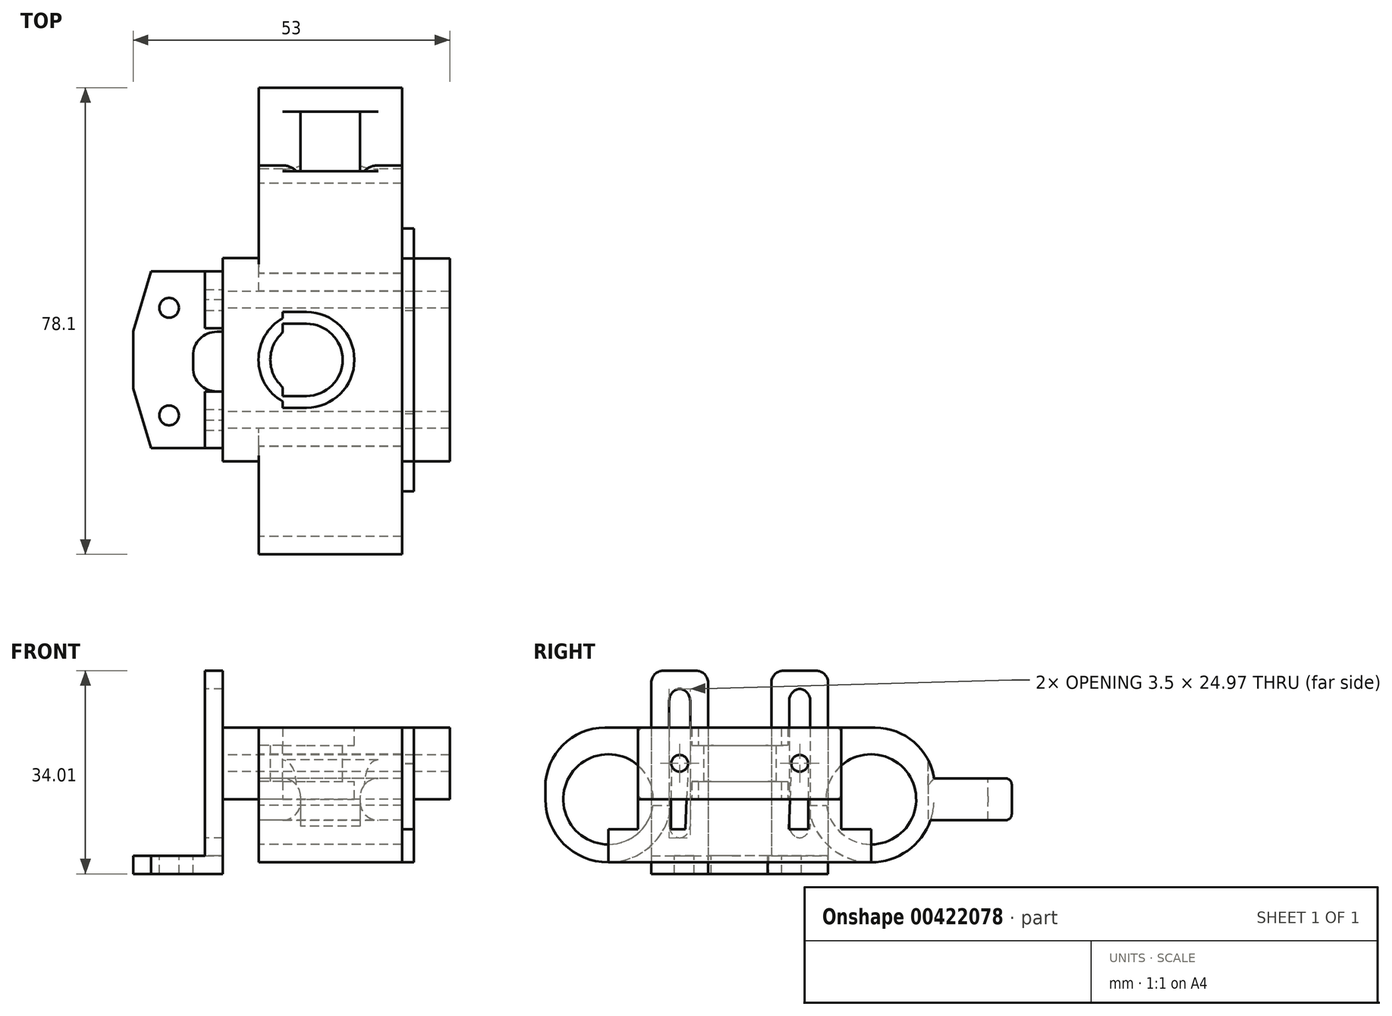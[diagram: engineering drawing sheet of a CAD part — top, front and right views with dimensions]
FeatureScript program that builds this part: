
annotation { "Feature Type Name" : "Feature", "Feature Type Description" : "" }
export const myFeature = defineFeature(function(context is Context, id is Id, definition is map)
    precondition{}
    {
        {
            var Q0;
            Q0=qCreatedBy(makeId("Right.planeOp"),FACE);
            var sketch = newSketch(context, id + "F0", { "sketchPlane" : qUnion([Q0])});
            skCircle(sketch, "E0", {"center": v(0, 0) * mm, "radius": 7.55 * mm});
            skCircle(sketch, "E1", {"center": v(44, 0) * mm, "radius": 7.55 * mm});
            skSolve(sketch);
        }
        {
            var Q0;
            Q0=makeQuery(id+"F0.imprint","IMPRINT",FACE,{"disambiguationData":[TD([[makeQuery(id+"F0.imprint","IMPRINT",EDGE,{"derivedFrom":sQuery(id+"F0.wireOp",EDGE,"E0")}),1.0]])]});
            var Q1;
            Q1=makeQuery(id+"F0.imprint","IMPRINT",FACE,{"disambiguationData":[TD([[makeQuery(id+"F0.imprint","IMPRINT",EDGE,{"derivedFrom":sQuery(id+"F0.wireOp",EDGE,"E1")}),1.0]])]});
            extrude(context, id + "F1", {"entities" : qUnion([Q0, Q1]), "depth" : 24 * mm});
        }
        {
            var Q0;
            Q0=qCreatedBy(makeId("Right.planeOp"),FACE);
            var sketch = newSketch(context, id + "F2", { "sketchPlane" : qUnion([Q0])});
            skCircle(sketch, "E2.0.0", {"center": v(0, 0) * mm, "radius": 7.55 * mm, "construction": true});
            skCircle(sketch, "E3.0.0", {"center": v(44, 0) * mm, "radius": 7.55 * mm, "construction": true});
            skLineSegment(sketch, "E4", {"start": v(7.55, 0) * mm, "end": v(22, 0) * mm, "construction": true});
            skLineSegment(sketch, "E5", {"start": v(22, 0) * mm, "end": v(36.45, 0) * mm, "construction": true});
            skLineSegment(sketch, "E6", {"start": v(22, 0) * mm, "end": v(22, 12.75) * mm});
            skLineSegment(sketch, "E7", {"start": v(22, 12.75) * mm, "end": v(13.97, 12.75) * mm});
            skLineSegment(sketch, "E8", {"start": v(13.97, 12.75) * mm, "end": v(13.97, 9.05) * mm});
            skLineSegment(sketch, "E9", {"start": v(13.97, 9.05) * mm, "end": v(15.95, 9.05) * mm});
            skLineSegment(sketch, "E10", {"start": v(15.95, 9.05) * mm, "end": v(15.95, 3) * mm});
            skLineSegment(sketch, "E11", {"start": v(15.95, 3) * mm, "end": v(13.98, 3) * mm});
            skLineSegment(sketch, "E12", {"start": v(13.97, 3) * mm, "end": v(13.97, 0) * mm});
            skLineSegment(sketch, "E13", {"start": v(13.98, 0) * mm, "end": v(22, 0) * mm});
            skSolve(sketch);
        }
        {
            var Q0;
            Q0=qCreatedBy(makeId("Right.planeOp"),FACE);
            var sketch = newSketch(context, id + "F3", { "sketchPlane" : qUnion([Q0])});
            skLineSegment(sketch, "E14", {"start": v(-10.55, 0) * mm, "end": v(54.55, 0) * mm});
            skLineSegment(sketch, "E15", {"start": v(54.55, 12) * mm, "end": v(-10.55, 12) * mm});
            skLineSegment(sketch, "E16", {"start": v(-10.55, 12) * mm, "end": v(-10.55, 0) * mm});
            skCircle(sketch, "E17.0", {"center": v(0, 0) * mm, "radius": 7.55 * mm, "construction": true});
            skCircle(sketch, "E18.0", {"center": v(44, 0) * mm, "radius": 7.55 * mm, "construction": true});
            skArc(sketch, "E19.0", {"start": v(33.45, 0) * mm, "mid": v(44, -10.55) * mm, "end": v(54.55, 0) * mm});
            skArc(sketch, "E20.0", {"start": v(-10.55, 0) * mm, "mid": v(0, -10.55) * mm, "end": v(10.55, 0) * mm});
            skLineSegment(sketch, "E21", {"start": v(54.55, 0) * mm, "end": v(54.55, 12) * mm});
            skLineSegment(sketch, "E22", {"start": v(54.55, 3.5) * mm, "end": v(67.55, 3.5) * mm});
            skLineSegment(sketch, "E23", {"start": v(67.55, 3.5) * mm, "end": v(67.55, -3.5) * mm});
            skLineSegment(sketch, "E24", {"start": v(67.55, -3.5) * mm, "end": v(53.95, -3.5) * mm});
            skSolve(sketch);
        }
        {
            var Q0;
            Q0 = qSketchRegion(id + "F3", true);
            extrude(context, id + "F4", {"entities" : qUnion([Q0]), "depth" : 24 * mm});
        }
        {
            var Q0;
            Q0 = qSketchRegion(id + "F0", true);
            var Q1;
            Q1 = qConstructionFilter(qBodyType(qCreatedBy(id + "F0" ,EDGE), BodyType.WIRE), ConstructionObject.NO);
            extrude(context, id + "F5", {"entities" : qUnion([Q0]), "operationType" : NewBodyOperationType.REMOVE, "surfaceEntities" : qUnion([Q1]), "endBound" : BoundingType.THROUGH_ALL, "depth" : 25 * mm});
        }
        {
            var Q0;
            Q0=qCreatedBy(makeId("Top.planeOp"),FACE);
            var sketch = newSketch(context, id + "F6", { "sketchPlane" : qUnion([Q0])});
            skLineSegment(sketch, "E25.0", {"start": v(0, 13.98) * mm, "end": v(0, 22) * mm, "construction": true});
            skLineSegment(sketch, "E26", {"start": v(0, 14) * mm, "end": v(8, 14) * mm});
            skLineSegment(sketch, "E27", {"start": v(8, 22) * mm, "end": v(0, 22) * mm, "construction": true});
            skLineSegment(sketch, "E28.MirrorCS", {"start": v(0, 30) * mm, "end": v(8, 30) * mm});
            skArc(sketch, "E29", {"start": v(8, 14) * mm, "mid": v(16, 22) * mm, "end": v(8, 30) * mm});
            skSolve(sketch);
        }
        {
            var Q0;
            Q0=makeQuery(id+"F2.imprint","IMPRINT",FACE,{"disambiguationData":[TD([[makeQuery(id+"F2.imprint","IMPRINT",EDGE,{"derivedFrom":sQuery(id+"F2.wireOp",EDGE,"E6")}),1.0]])]});
            var Q1;
            Q1=sQuery(id+"F6.wireOp",EDGE,"E26");
            var Q2;
            Q2=sQuery(id+"F6.wireOp",EDGE,"E29");
            var Q3;
            Q3=sQuery(id+"F6.wireOp",EDGE,"E28.MirrorCS");
            sweep(context, id + "F7", {"operationType" : NewBodyOperationType.REMOVE, "profiles" : qUnion([Q0]), "path" : qUnion([Q1, Q2, Q3])});
        }
        {
            var Q0;
            Q0=makeQuery(id+"F4.opExtrude","SWEPT_FACE",FACE,{"disambiguationData":[OSD([sQuery(id+"F3.wireOp",EDGE,"E15")])]});
            var sketch = newSketch(context, id + "F8", { "sketchPlane" : qUnion([Q0])});
            skLineSegment(sketch, "E30.0", {"start": v(25, -7.5) * mm, "end": v(0, -7.5) * mm});
            skLineSegment(sketch, "E31.0", {"start": v(25, -13.5) * mm, "end": v(0, -13.5) * mm, "construction": true});
            skLineSegment(sketch, "E32.0", {"start": v(24, -13.5) * mm, "end": v(24, -7.5) * mm, "construction": true});
            skLineSegment(sketch, "E33.0", {"start": v(0, -13.5) * mm, "end": v(0, -7.5) * mm, "construction": true});
            skLineSegment(sketch, "E34", {"start": v(25, -10.5) * mm, "end": v(20, -10.5) * mm, "construction": true});
            skLineSegment(sketch, "E35", {"start": v(20, -10.5) * mm, "end": v(5, -10.5) * mm, "construction": true});
            skLineSegment(sketch, "E36", {"start": v(5, -10.5) * mm, "end": v(0, -10.5) * mm, "construction": true});
            skLineSegment(sketch, "E37", {"start": v(25, -7.5) * mm, "end": v(25, 62.5) * mm, "construction": true});
            skLineSegment(sketch, "E38", {"start": v(25, 0) * mm, "end": v(0, 0) * mm, "construction": true});
            skLineSegment(sketch, "E39.MirrorCS", {"start": v(25, 7.5) * mm, "end": v(0, 7.5) * mm, "construction": true});
            skLineSegment(sketch, "E40.MirrorCS", {"start": v(20, 10.5) * mm, "end": v(5, 10.5) * mm, "construction": true});
            skPoint(sketch, "E41.0", {"position": v(14.05, 22) * mm});
            skPoint(sketch, "E42.0", {"position": v(16.03, 22) * mm});
            skLineSegment(sketch, "E43", {"start": v(16, 22) * mm, "end": v(14, 22) * mm, "construction": true});
            skLineSegment(sketch, "E44.MirrorCS", {"start": v(20, 33.5) * mm, "end": v(5, 33.5) * mm, "construction": true});
            skLineSegment(sketch, "E45.MirrorCS", {"start": v(20, 54.5) * mm, "end": v(5, 54.5) * mm, "construction": true});
            skSolve(sketch);
        }
        {
            var Q0;
            Q0=makeQuery(id+"F4.opExtrude","SWEPT_EDGE",EDGE,{"disambiguationData":[OSD([sQuery(id+"F3.wireOp",EDGE,"E15"),sQuery(id+"F3.wireOp",EDGE,"E21")])]});
            var Q1;
            Q1=makeQuery(id+"F4.opExtrude","SWEPT_EDGE",EDGE,{"disambiguationData":[OSD([sQuery(id+"F3.wireOp",EDGE,"E15"),sQuery(id+"F3.wireOp",EDGE,"E16")])]});
            fillet(context, id + "F9", {"entities" : qUnion([Q0, Q1]), "radius" : 10 * mm, "tangentPropagation" : true, "allowEdgeOverflow" : false});
        }
        {
            var Q0;
            {var subQ1=sQuery(id+"F3.wireOp",EDGE,"E24");var subQ2=sQuery(id+"F3.wireOp",EDGE,"E23");var subQ4=sQuery(id+"F3.wireOp",EDGE,"E22");var subQ5=sQuery(id+"F3.wireOp",EDGE,"E14");var subQ6=sQuery(id+"F3.wireOp",EDGE,"E19.0");var subQ7=sQuery(id+"F3.wireOp",EDGE,"E15");var subQ8=sQuery(id+"F3.wireOp",EDGE,"E21");Q0=makeQuery(id+"F7.boolean.opBoolean","SPLIT",FACE,{"disambiguationData":[TD([makeQuery(id+"F4.opExtrude","SWEPT_FACE",FACE,{"disambiguationData":[OSD([subQ6])]})])],"derivedFrom":makeQuery(id+"F4.opExtrude","CAP_FACE",FACE,{"disambiguationData":[OSD([subQ5,subQ7,sQuery(id+"F3.wireOp",EDGE,"E16"),subQ6,sQuery(id+"F3.wireOp",EDGE,"E20.0"),subQ8,subQ4,subQ2,subQ1])],"isStart":true})});}
            var sketch = newSketch(context, id + "F10", { "sketchPlane" : qUnion([Q0])});
            skLineSegment(sketch, "E46.bottom", {"start": v(-4.98, 0) * mm, "end": v(-39.02, 0) * mm});
            skLineSegment(sketch, "E46.top", {"start": v(-4.98, 12) * mm, "end": v(-39.02, 12) * mm});
            skLineSegment(sketch, "E46.left", {"start": v(-4.97, 0) * mm, "end": v(-4.98, 12) * mm});
            skLineSegment(sketch, "E46.right", {"start": v(-39.02, 0) * mm, "end": v(-39.02, 12) * mm});
            skLineSegment(sketch, "E47.0", {"start": v(-30.02, 3) * mm, "end": v(-30.02, 0) * mm});
            skLineSegment(sketch, "E48.0", {"start": v(-28.05, 3) * mm, "end": v(-30.02, 3) * mm});
            skLineSegment(sketch, "E49.0", {"start": v(-28.05, 9.05) * mm, "end": v(-28.05, 3) * mm});
            skLineSegment(sketch, "E50.0", {"start": v(-30.02, 9.05) * mm, "end": v(-28.05, 9.05) * mm});
            skLineSegment(sketch, "E51.0", {"start": v(-30.02, 12) * mm, "end": v(-30.02, 9.05) * mm});
            skLineSegment(sketch, "E52.0", {"start": v(-13.97, 12) * mm, "end": v(-13.97, 9.05) * mm});
            skLineSegment(sketch, "E53.0", {"start": v(-13.97, 9.05) * mm, "end": v(-15.95, 9.05) * mm});
            skLineSegment(sketch, "E54.0", {"start": v(-15.95, 9.05) * mm, "end": v(-15.95, 3) * mm});
            skLineSegment(sketch, "E55.0", {"start": v(-15.95, 3) * mm, "end": v(-13.98, 3) * mm});
            skLineSegment(sketch, "E56.0", {"start": v(-13.97, 3) * mm, "end": v(-13.97, 0) * mm});
            skSolve(sketch);
        }
        {
            var Q0;
            {var subQ2=sQuery(id+"F10.wireOp",EDGE,"E47.0");Q0=makeQuery(id+"F10.imprint","IMPRINT",FACE,{"disambiguationData":[TD([[makeQuery(id+"F10.imprint","IMPRINT",EDGE,{"derivedFrom":subQ2}),1.0]])]});}
            extrude(context, id + "F11", {"entities" : qUnion([Q0]), "oppositeDirection" : true, "depth" : 4 * mm});
        }
        {
            var Q0;
            Q0=qCreatedBy(makeId("Right.planeOp"),FACE);
            cPlane(context, id + "F12", {"entities" : qUnion([Q0]), "cplaneType" : CPlaneType.OFFSET, "offset" : 8 * mm, "width" : 150 * mm, "height" : 150 * mm});
        }
        {
            var Q0;
            {var subQ2=sQuery(id+"F10.wireOp",EDGE,"E47.0");Q0=makeQuery(id+"F10.imprint","IMPRINT",FACE,{"disambiguationData":[TD([[makeQuery(id+"F10.imprint","IMPRINT",EDGE,{"derivedFrom":subQ2}),1.0]])]});}
            var Q1;
            {var subQ2=sQuery(id+"F10.wireOp",EDGE,"E46.right");Q1=makeQuery(id+"F10.imprint","IMPRINT",FACE,{"disambiguationData":[TD([[makeQuery(id+"F10.imprint","IMPRINT",EDGE,{"derivedFrom":subQ2}),-1.0]])]});}
            var Q2;
            {var subQ0=sQuery(id+"F10.wireOp",EDGE,"E46.left");Q2=makeQuery(id+"F10.imprint","IMPRINT",FACE,{"disambiguationData":[TD([[makeQuery(id+"F10.imprint","IMPRINT",EDGE,{"derivedFrom":subQ0}),1.0]])]});}
            var Q3;
            {var subQ12=sQuery(id+"F10.wireOp",EDGE,"E47.0");Q3=makeQuery(id+"F10.imprint","IMPRINT",FACE,{"disambiguationData":[TD([[makeQuery(id+"F10.imprint","IMPRINT",EDGE,{"derivedFrom":subQ12}),-1.0]])]});}
            extrude(context, id + "F13", {"entities" : qUnion([Q0, Q1, Q2, Q3]), "operationType" : NewBodyOperationType.ADD, "depth" : 6 * mm});
        }
        {
            var Q0;
            Q0=qCreatedBy(id+"F12.planeOp",FACE);
            var sketch = newSketch(context, id + "F14", { "sketchPlane" : qUnion([Q0])});
            skLineSegment(sketch, "E57.0", {"start": v(13.97, 12) * mm, "end": v(13.97, 9.05) * mm});
            skPoint(sketch, "E58.0", {"position": v(22, 12) * mm});
            skPoint(sketch, "E59.0", {"position": v(22, 0) * mm});
            skLineSegment(sketch, "E60.0", {"start": v(13.97, 9.05) * mm, "end": v(15.95, 9.05) * mm});
            skLineSegment(sketch, "E60.1", {"start": v(15.95, 9.05) * mm, "end": v(15.95, 3) * mm});
            skLineSegment(sketch, "E60.2", {"start": v(15.95, 3) * mm, "end": v(13.98, 3) * mm});
            skLineSegment(sketch, "E61", {"start": v(22, 0) * mm, "end": v(13.97, 0) * mm});
            skLineSegment(sketch, "E62", {"start": v(13.97, 0) * mm, "end": v(13.97, 3) * mm});
            skLineSegment(sketch, "E63", {"start": v(22, 0) * mm, "end": v(22, 12) * mm});
            skLineSegment(sketch, "E64", {"start": v(22, 12) * mm, "end": v(13.97, 12) * mm});
            skSolve(sketch);
        }
        {
            var Q0;
            Q0=makeQuery(id+"F14.imprint","IMPRINT",FACE,{"disambiguationData":[TD([[makeQuery(id+"F14.imprint","IMPRINT",EDGE,{"derivedFrom":sQuery(id+"F14.wireOp",EDGE,"E57.0")}),1.0]])]});
            var Q1;
            Q1=sQuery(id+"F14.wireOp",EDGE,"E63");
            revolve(context, id + "F15", {"operationType" : NewBodyOperationType.REMOVE, "entities" : qUnion([Q0]), "axis" : qUnion([Q1]), "revolveType" : RevolveType.FULL});
        }
        {
            var Q0;
            Q0=makeQuery(id+"F13.opExtrude","CAP_FACE",FACE,{"disambiguationData":[OSD([sQuery(id+"F10.wireOp",EDGE,"E46.bottom"),sQuery(id+"F10.wireOp",EDGE,"E46.top"),sQuery(id+"F10.wireOp",EDGE,"E46.left"),sQuery(id+"F10.wireOp",EDGE,"E46.right")])],"isStart":false});
            var sketch = newSketch(context, id + "F16", { "sketchPlane" : qUnion([Q0])});
            skLineSegment(sketch, "E65.0", {"start": v(-15.95, 9.05) * mm, "end": v(-15.95, 3) * mm});
            skLineSegment(sketch, "E66.0", {"start": v(-28.05, 9.05) * mm, "end": v(-28.05, 3) * mm});
            skLineSegment(sketch, "E67", {"start": v(-15.95, 6.03) * mm, "end": v(-28.05, 6.03) * mm});
            skLineSegment(sketch, "E68", {"start": v(-28.05, 6.03) * mm, "end": v(-32.05, 6.03) * mm});
            skLineSegment(sketch, "E69", {"start": v(-15.95, 6.03) * mm, "end": v(-11.95, 6.03) * mm});
            skSolve(sketch);
        }
        {
            var Q0;
            Q0=sQuery(id+"F16.wireOp",VERTEX,"kSKMyoxM-GP1p-jTyX-dCB2-GsyD5X9PXskR.end");
            var Q1;
            Q1=sQuery(id+"F16.wireOp",VERTEX,"UNS4y3Tf-MKdk-kDcg-mpHp-VkzCvE5mjTKt.end");
            var Q2;
            Q2=sQuery(id+"F16.wireOp",VERTEX,"E69.end");
            var Q3;
            Q3=sQuery(id+"F16.wireOp",VERTEX,"E68.end");
            var Q4;
            Q4=makeQuery(id+"F4.opExtrude","SWEPT_BODY",BODY,{"disambiguationData":[OSD([sQuery(id+"F3.wireOp",EDGE,"E14"),sQuery(id+"F3.wireOp",EDGE,"k89EXZ4l-FsP1-d0Dv-wgbo-ABCzMf410Jy9"),sQuery(id+"F3.wireOp",EDGE,"90tfrgYt-6Hfx-LERH-6RQe-psnA0FiorwHZ"),sQuery(id+"F3.wireOp",EDGE,"E15"),sQuery(id+"F3.wireOp",EDGE,"E16"),sQuery(id+"F3.wireOp",EDGE,"xU4Ry4fZ-u7LB-lCky-6Ndd-EhexzLKnma8q")])]});
            var Q5;
            Q5=makeQuery(id+"F11.opExtrude","SWEPT_BODY",BODY,{"disambiguationData":[OSD([sQuery(id+"F10.wireOp",EDGE,"E46.bottom"),sQuery(id+"F10.wireOp",EDGE,"E46.top"),sQuery(id+"F10.wireOp",EDGE,"E47.0"),sQuery(id+"F10.wireOp",EDGE,"E48.0"),sQuery(id+"F10.wireOp",EDGE,"E49.0"),sQuery(id+"F10.wireOp",EDGE,"E50.0"),sQuery(id+"F10.wireOp",EDGE,"E51.0"),sQuery(id+"F10.wireOp",EDGE,"E52.0"),sQuery(id+"F10.wireOp",EDGE,"E53.0"),sQuery(id+"F10.wireOp",EDGE,"E54.0"),sQuery(id+"F10.wireOp",EDGE,"E55.0"),sQuery(id+"F10.wireOp",EDGE,"E56.0")])]});
            hole(context, id + "F17", {"style" : HoleStyle.SIMPLE, "endStyle" : HoleEndStyle.THROUGH, "holeDiameter" : 2.8 * mm, "isTappedThrough" : true, "tappedDepth" : 12 * mm, "tapClearance" : 3, "locations" : qUnion([Q0, Q1, Q2, Q3]), "scope" : qUnion([Q4, Q5])});
        }
        {
            var Q0;
            Q0=makeQuery(id+"F13.opExtrude","CAP_FACE",FACE,{"disambiguationData":[OSD([sQuery(id+"F10.wireOp",EDGE,"E46.bottom"),sQuery(id+"F10.wireOp",EDGE,"E46.top"),sQuery(id+"F10.wireOp",EDGE,"E46.left"),sQuery(id+"F10.wireOp",EDGE,"E46.right")])],"isStart":false});
            var sketch = newSketch(context, id + "F18", { "sketchPlane" : qUnion([Q0])});
            skCircle(sketch, "E70.0", {"center": v(-32.05, 6.03) * mm, "radius": 1.4 * mm, "construction": true});
            skCircle(sketch, "E71.0", {"center": v(-11.95, 6.03) * mm, "radius": 1.4 * mm, "construction": true});
            skLineSegment(sketch, "E72.bottom", {"start": v(-30.3, 18.52) * mm, "end": v(-33.8, 18.52) * mm});
            skLineSegment(sketch, "E72.top", {"start": v(-30.3, -6.47) * mm, "end": v(-33.8, -6.47) * mm});
            skLineSegment(sketch, "E72.left", {"start": v(-30.3, 18.53) * mm, "end": v(-30.3, -6.48) * mm});
            skLineSegment(sketch, "E72.right", {"start": v(-33.8, 18.52) * mm, "end": v(-33.8, -6.47) * mm});
            skLineSegment(sketch, "E73", {"start": v(-32.05, 6.03) * mm, "end": v(-22, 6.03) * mm, "construction": true});
            skLineSegment(sketch, "E74", {"start": v(-22, 6.03) * mm, "end": v(-11.95, 6.03) * mm, "construction": true});
            skLineSegment(sketch, "E75", {"start": v(-22, 6.03) * mm, "end": v(-22, 14.16) * mm, "construction": true});
            skLineSegment(sketch, "E76.0", {"start": v(-27.3, 21.52) * mm, "end": v(-36.8, 21.52) * mm});
            skLineSegment(sketch, "E76.1", {"start": v(-27.3, 21.52) * mm, "end": v(-27.3, -9.47) * mm});
            skLineSegment(sketch, "E76.2", {"start": v(-27.3, -9.47) * mm, "end": v(-36.8, -9.47) * mm});
            skLineSegment(sketch, "E76.3", {"start": v(-36.8, 21.52) * mm, "end": v(-36.8, -9.48) * mm});
            skLineSegment(sketch, "E77.MirrorCS", {"start": v(-13.7, 18.53) * mm, "end": v(-13.7, -6.47) * mm});
            skLineSegment(sketch, "E78.MirrorCS", {"start": v(-10.2, 18.53) * mm, "end": v(-10.2, -6.47) * mm});
            skLineSegment(sketch, "E79.MirrorCS", {"start": v(-13.7, 18.53) * mm, "end": v(-10.2, 18.53) * mm});
            skLineSegment(sketch, "E80.MirrorCS", {"start": v(-13.7, -6.47) * mm, "end": v(-10.2, -6.47) * mm});
            skLineSegment(sketch, "E81.MirrorCS", {"start": v(-16.7, -9.47) * mm, "end": v(-7.2, -9.47) * mm});
            skLineSegment(sketch, "E82.MirrorCS", {"start": v(-16.7, 21.53) * mm, "end": v(-16.7, -9.47) * mm});
            skLineSegment(sketch, "E83.MirrorCS", {"start": v(-7.2, 21.53) * mm, "end": v(-7.2, -9.47) * mm});
            skLineSegment(sketch, "E84.MirrorCS", {"start": v(-16.7, 21.52) * mm, "end": v(-7.2, 21.53) * mm});
            skLineSegment(sketch, "E85.bottom", {"start": v(-36.8, -9.48) * mm, "end": v(-7.2, -9.48) * mm});
            skLineSegment(sketch, "E85.top", {"start": v(-36.8, -12.47) * mm, "end": v(-7.2, -12.47) * mm});
            skLineSegment(sketch, "E85.left", {"start": v(-36.8, -9.48) * mm, "end": v(-36.8, -12.47) * mm});
            skLineSegment(sketch, "E85.right", {"start": v(-7.2, -9.47) * mm, "end": v(-7.2, -12.47) * mm});
            skSolve(sketch);
        }
        {
            var Q0;
            {var subQ9=sQuery(id+"F18.wireOp",EDGE,"E79.MirrorCS");Q0=makeQuery(id+"F18.imprint","IMPRINT",FACE,{"disambiguationData":[TD([[makeQuery(id+"F18.imprint","IMPRINT",EDGE,{"derivedFrom":subQ9}),1.0]])]});}
            var Q1;
            {var subQ0=sQuery(id+"F18.wireOp",EDGE,"E77.MirrorCS");var subQ1=makeQuery(id+"F13.opExtrude","CAP_EDGE",EDGE,{"disambiguationData":[OSD([sQuery(id+"F10.wireOp",EDGE,"E46.top")])],"isStart":false});var subQ2=makeQuery(id+"F18.imprint","INTERSECT",VERTEX,{"derivedFrom":[subQ1,subQ0]});Q1=makeQuery(id+"F18.imprint","IMPRINT",FACE,{"disambiguationData":[TD([[makeQuery(id+"F18.imprint","IMPRINT",EDGE,{"disambiguationData":[TD([[subQ2,-1.0]])],"derivedFrom":subQ0}),-1.0]])]});}
            var Q2;
            {var subQ0=sQuery(id+"F18.wireOp",EDGE,"E72.left");var subQ1=makeQuery(id+"F13.opExtrude","CAP_EDGE",EDGE,{"disambiguationData":[OSD([sQuery(id+"F10.wireOp",EDGE,"E46.top")])],"isStart":false});var subQ2=makeQuery(id+"F18.imprint","INTERSECT",VERTEX,{"derivedFrom":[subQ1,subQ0]});Q2=makeQuery(id+"F18.imprint","IMPRINT",FACE,{"disambiguationData":[TD([[makeQuery(id+"F18.imprint","IMPRINT",EDGE,{"disambiguationData":[TD([[subQ2,-1.0]])],"derivedFrom":subQ0}),1.0]])]});}
            var Q3;
            {var subQ8=sQuery(id+"F18.wireOp",EDGE,"E72.bottom");Q3=makeQuery(id+"F18.imprint","IMPRINT",FACE,{"disambiguationData":[TD([[makeQuery(id+"F18.imprint","IMPRINT",EDGE,{"derivedFrom":subQ8}),-1.0]])]});}
            var Q4;
            Q4=makeQuery(id+"F18.imprint","IMPRINT",FACE,{"disambiguationData":[TD([[makeQuery(id+"F18.imprint","IMPRINT",EDGE,{"derivedFrom":sQuery(id+"F18.wireOp",EDGE,"E85.top")}),1.0]])]});
            var Q5;
            {var subQ0=sQuery(id+"F18.wireOp",EDGE,"E72.right");var subQ1=makeQuery(id+"F13.opExtrude","CAP_EDGE",EDGE,{"disambiguationData":[OSD([sQuery(id+"F10.wireOp",EDGE,"E46.top")])],"isStart":false});var subQ2=makeQuery(id+"F18.imprint","INTERSECT",VERTEX,{"derivedFrom":[subQ1,subQ0]});Q5=makeQuery(id+"F18.imprint","IMPRINT",FACE,{"disambiguationData":[TD([[makeQuery(id+"F18.imprint","IMPRINT",EDGE,{"disambiguationData":[TD([[subQ2,-1.0]])],"derivedFrom":subQ0}),-1.0]])]});}
            var Q6;
            {var subQ0=sQuery(id+"F18.wireOp",EDGE,"E78.MirrorCS");var subQ1=makeQuery(id+"F13.opExtrude","CAP_EDGE",EDGE,{"disambiguationData":[OSD([sQuery(id+"F10.wireOp",EDGE,"E46.top")])],"isStart":false});var subQ2=makeQuery(id+"F18.imprint","INTERSECT",VERTEX,{"derivedFrom":[subQ1,subQ0]});Q6=makeQuery(id+"F18.imprint","IMPRINT",FACE,{"disambiguationData":[TD([[makeQuery(id+"F18.imprint","IMPRINT",EDGE,{"disambiguationData":[TD([[subQ2,-1.0]])],"derivedFrom":subQ0}),1.0]])]});}
            var Q7;
            {var subQ5=sQuery(id+"F18.wireOp",EDGE,"E80.MirrorCS");Q7=makeQuery(id+"F18.imprint","IMPRINT",FACE,{"disambiguationData":[TD([[makeQuery(id+"F18.imprint","IMPRINT",EDGE,{"derivedFrom":subQ5}),-1.0]])]});}
            var Q8;
            {var subQ1=sQuery(id+"F18.wireOp",EDGE,"E72.top");Q8=makeQuery(id+"F18.imprint","IMPRINT",FACE,{"disambiguationData":[TD([[makeQuery(id+"F18.imprint","IMPRINT",EDGE,{"derivedFrom":subQ1}),1.0]])]});}
            extrude(context, id + "F19", {"entities" : qUnion([Q0, Q1, Q2, Q3, Q4, Q5, Q6, Q7, Q8]), "depth" : 3 * mm});
        }
        {
            var Q0;
            Q0=makeQuery(id+"F18.imprint","IMPRINT",FACE,{"disambiguationData":[TD([[makeQuery(id+"F18.imprint","IMPRINT",EDGE,{"derivedFrom":sQuery(id+"F18.wireOp",EDGE,"E85.top")}),1.0]])]});
            extrude(context, id + "F20", {"entities" : qUnion([Q0]), "operationType" : NewBodyOperationType.ADD, "depth" : 15 * mm});
        }
        {
            var Q0;
            {var subQ0=sQuery(id+"F18.wireOp",EDGE,"E85.bottom");Q0=makeQuery(id+"F20.boolean.opBoolean","MERGE",FACE,{"derivedFrom":[makeQuery(id+"F19.opExtrude","SWEPT_FACE",FACE,{"disambiguationData":[OSD([subQ0])]}),makeQuery(id+"F20.opExtrude","SWEPT_FACE",FACE,{"disambiguationData":[OSD([subQ0])]})]});}
            var sketch = newSketch(context, id + "F21", { "sketchPlane" : qUnion([Q0])});
            skLineSegment(sketch, "E86.bottom", {"start": v(-6, 16.7) * mm, "end": v(-11, 16.7) * mm});
            skLineSegment(sketch, "E86.top", {"start": v(-6, 26.7) * mm, "end": v(-11, 26.7) * mm});
            skLineSegment(sketch, "E86.left", {"start": v(-6, 16.7) * mm, "end": v(-6, 26.7) * mm});
            skLineSegment(sketch, "E86.right", {"start": v(-11, 16.7) * mm, "end": v(-11, 26.7) * mm});
            skSolve(sketch);
        }
        {
            var Q0;
            Q0=makeQuery(id+"F21.imprint","IMPRINT",FACE,{"disambiguationData":[TD([[makeQuery(id+"F21.imprint","IMPRINT",EDGE,{"derivedFrom":sQuery(id+"F21.wireOp",EDGE,"E86.bottom")}),1.0]])]});
            extrude(context, id + "F22", {"entities" : qUnion([Q0]), "operationType" : NewBodyOperationType.REMOVE, "oppositeDirection" : true, "depth" : 25 * mm});
        }
        {
            var Q0;
            Q0=makeQuery(id+"F19.opExtrude","SWEPT_EDGE",EDGE,{"disambiguationData":[OSD([sQuery(id+"F18.wireOp",EDGE,"E76.0"),sQuery(id+"F18.wireOp",EDGE,"E76.3")])]});
            var Q1;
            Q1=makeQuery(id+"F19.opExtrude","SWEPT_EDGE",EDGE,{"disambiguationData":[OSD([sQuery(id+"F18.wireOp",EDGE,"E76.0"),sQuery(id+"F18.wireOp",EDGE,"E76.1")])]});
            var Q2;
            Q2=makeQuery(id+"F19.opExtrude","SWEPT_EDGE",EDGE,{"disambiguationData":[OSD([sQuery(id+"F18.wireOp",EDGE,"E82.MirrorCS"),sQuery(id+"F18.wireOp",EDGE,"E84.MirrorCS")])]});
            var Q3;
            Q3=makeQuery(id+"F19.opExtrude","SWEPT_EDGE",EDGE,{"disambiguationData":[OSD([sQuery(id+"F18.wireOp",EDGE,"E83.MirrorCS"),sQuery(id+"F18.wireOp",EDGE,"E84.MirrorCS")])]});
            var Q4;
            Q4=makeQuery(id+"F19.opExtrude","SWEPT_EDGE",EDGE,{"disambiguationData":[OSD([sQuery(id+"F18.wireOp",EDGE,"E78.MirrorCS"),sQuery(id+"F18.wireOp",EDGE,"E80.MirrorCS")])]});
            var Q5;
            Q5=makeQuery(id+"F19.opExtrude","SWEPT_EDGE",EDGE,{"disambiguationData":[OSD([sQuery(id+"F18.wireOp",EDGE,"E77.MirrorCS"),sQuery(id+"F18.wireOp",EDGE,"E80.MirrorCS")])]});
            var Q6;
            Q6=makeQuery(id+"F19.opExtrude","SWEPT_EDGE",EDGE,{"disambiguationData":[OSD([sQuery(id+"F18.wireOp",EDGE,"E72.top"),sQuery(id+"F18.wireOp",EDGE,"E72.left")])]});
            var Q7;
            Q7=makeQuery(id+"F19.opExtrude","SWEPT_EDGE",EDGE,{"disambiguationData":[OSD([sQuery(id+"F18.wireOp",EDGE,"E72.top"),sQuery(id+"F18.wireOp",EDGE,"E72.right")])]});
            var Q8;
            Q8=makeQuery(id+"F19.opExtrude","SWEPT_EDGE",EDGE,{"disambiguationData":[OSD([sQuery(id+"F18.wireOp",EDGE,"E77.MirrorCS"),sQuery(id+"F18.wireOp",EDGE,"E79.MirrorCS")])]});
            var Q9;
            Q9=makeQuery(id+"F19.opExtrude","SWEPT_EDGE",EDGE,{"disambiguationData":[OSD([sQuery(id+"F18.wireOp",EDGE,"E72.bottom"),sQuery(id+"F18.wireOp",EDGE,"E72.right")])]});
            var Q10;
            Q10=makeQuery(id+"F19.opExtrude","SWEPT_EDGE",EDGE,{"disambiguationData":[OSD([sQuery(id+"F18.wireOp",EDGE,"E78.MirrorCS"),sQuery(id+"F18.wireOp",EDGE,"E79.MirrorCS")])]});
            var Q11;
            Q11=makeQuery(id+"F19.opExtrude","SWEPT_EDGE",EDGE,{"disambiguationData":[OSD([sQuery(id+"F18.wireOp",EDGE,"E72.bottom"),sQuery(id+"F18.wireOp",EDGE,"E72.left")])]});
            fillet(context, id + "F23", {"entities" : qUnion([Q0, Q1, Q2, Q3, Q4, Q5, Q6, Q7, Q8, Q9, Q10, Q11]), "radius" : 2 * mm, "tangentPropagation" : true, "allowEdgeOverflow" : false});
        }
        {
            var Q0;
            Q0=makeQuery(id+"F22.boolean.opBoolean","COPY",EDGE,{"derivedFrom":makeQuery(id+"F22.opExtrude","SWEPT_EDGE",EDGE,{"disambiguationData":[OSD([sQuery(id+"F21.wireOp",EDGE,"E86.bottom"),sQuery(id+"F21.wireOp",EDGE,"E86.right")])]})});
            var Q1;
            Q1=makeQuery(id+"F22.boolean.opBoolean","COPY",EDGE,{"derivedFrom":makeQuery(id+"F22.opExtrude","SWEPT_EDGE",EDGE,{"disambiguationData":[OSD([sQuery(id+"F21.wireOp",EDGE,"E86.top"),sQuery(id+"F21.wireOp",EDGE,"E86.right")])]})});
            fillet(context, id + "F24", {"entities" : qUnion([Q0, Q1]), "radius" : 4 * mm, "tangentPropagation" : true, "allowEdgeOverflow" : false});
        }
        {
            var Q0;
            {var subQ0=sQuery(id+"F18.wireOp",EDGE,"E85.bottom");Q0=makeQuery(id+"F20.boolean.opBoolean","MERGE",FACE,{"derivedFrom":[makeQuery(id+"F19.opExtrude","SWEPT_FACE",FACE,{"disambiguationData":[OSD([subQ0])]}),makeQuery(id+"F20.opExtrude","SWEPT_FACE",FACE,{"disambiguationData":[OSD([subQ0])]})]});}
            var sketch = newSketch(context, id + "F25", { "sketchPlane" : qUnion([Q0])});
            skPoint(sketch, "E87.endSnap0", {"position": v(-11, 21.7) * mm});
            skLineSegment(sketch, "E88", {"start": v(-11, 21.7) * mm, "end": v(-21, 21.7) * mm});
            skPoint(sketch, "E88.endSnap0", {"position": v(-21, 22) * mm});
            skLineSegment(sketch, "E89", {"start": v(-15, 21.7) * mm, "end": v(-15, 30.7) * mm});
            skLineSegment(sketch, "E90", {"start": v(-15, 21.7) * mm, "end": v(-15, 12.7) * mm});
            skSolve(sketch);
        }
        {
            var Q0;
            Q0=sQuery(id+"F25.wireOp",VERTEX,"ZJJVFUzE-h6Nm-UuaI-t9hB-cUuJ78KFn35s.end");
            var Q1;
            Q1=sQuery(id+"F25.wireOp",VERTEX,"zJxwGRLg-Bzh0-VdJe-SVjD-cFLvOnwve59r.end");
            var Q2;
            Q2=sQuery(id+"F25.wireOp",VERTEX,"E89.end");
            var Q3;
            Q3=sQuery(id+"F25.wireOp",VERTEX,"E90.end");
            var Q4;
            Q4=makeQuery(id+"F19.opExtrude","SWEPT_BODY",BODY,{"disambiguationData":[OSD([sQuery(id+"F18.wireOp",EDGE,"E72.bottom"),sQuery(id+"F18.wireOp",EDGE,"E72.top"),sQuery(id+"F18.wireOp",EDGE,"E72.left"),sQuery(id+"F18.wireOp",EDGE,"E72.right"),sQuery(id+"F18.wireOp",EDGE,"E76.0"),sQuery(id+"F18.wireOp",EDGE,"E76.1"),sQuery(id+"F18.wireOp",EDGE,"E76.3"),sQuery(id+"F18.wireOp",EDGE,"E77.MirrorCS"),sQuery(id+"F18.wireOp",EDGE,"E78.MirrorCS"),sQuery(id+"F18.wireOp",EDGE,"E79.MirrorCS"),sQuery(id+"F18.wireOp",EDGE,"E80.MirrorCS"),sQuery(id+"F18.wireOp",EDGE,"E82.MirrorCS"),sQuery(id+"F18.wireOp",EDGE,"E83.MirrorCS"),sQuery(id+"F18.wireOp",EDGE,"E84.MirrorCS"),sQuery(id+"F18.wireOp",EDGE,"E85.bottom"),sQuery(id+"F18.wireOp",EDGE,"E85.top"),sQuery(id+"F18.wireOp",EDGE,"E85.left"),sQuery(id+"F18.wireOp",EDGE,"E85.right")])]});
            hole(context, id + "F26", {"style" : HoleStyle.SIMPLE, "endStyle" : HoleEndStyle.THROUGH, "standardTappedOrClearance" : lookupTablePath({ "standard" : "ISO", "fit" : "Normal", "size" : "M3", "type" : "Clearance" }), "standardBlindInLast" : lookupTablePath({ "fit" : "Standard", "standard" : "ISO", "size" : "M3", "type" : "Clearance" }), "holeDiameter" : 3.3 * mm, "isTappedThrough" : true, "tappedDepth" : 12 * mm, "tapClearance" : 3, "locations" : qUnion([Q0, Q1, Q2, Q3]), "scope" : qUnion([Q4])});
        }
        {
            var Q0;
            Q0=makeQuery(id+"F20.opExtrude","CAP_EDGE",EDGE,{"disambiguationData":[OSD([sQuery(id+"F18.wireOp",EDGE,"E85.right")])],"isStart":false});
            var Q1;
            Q1=makeQuery(id+"F20.opExtrude","CAP_EDGE",EDGE,{"disambiguationData":[OSD([sQuery(id+"F18.wireOp",EDGE,"E85.left")])],"isStart":false});
            chamfer(context, id + "F27", {"entities" : qUnion([Q0, Q1]), "chamferType" : ChamferType.TWO_OFFSETS, "width1" : 3 * mm, "oppositeDirection" : false, "width2" : 10 * mm, "tangentPropagation" : true});
        }
        {
            var Q0;
            Q0=makeQuery(id+"F4.opExtrude","CAP_FACE",FACE,{"disambiguationData":[OSD([sQuery(id+"F3.wireOp",EDGE,"E14"),sQuery(id+"F3.wireOp",EDGE,"E15"),sQuery(id+"F3.wireOp",EDGE,"E16"),sQuery(id+"F3.wireOp",EDGE,"E19.0"),sQuery(id+"F3.wireOp",EDGE,"E20.0"),sQuery(id+"F3.wireOp",EDGE,"E21"),sQuery(id+"F3.wireOp",EDGE,"E22"),sQuery(id+"F3.wireOp",EDGE,"E23"),sQuery(id+"F3.wireOp",EDGE,"E24")])],"isStart":false});
            var sketch = newSketch(context, id + "F28", { "sketchPlane" : qUnion([Q0])});
            skLineSegment(sketch, "E91", {"start": v(0, 0) * mm, "end": v(44, 0) * mm, "construction": true});
            skLineSegment(sketch, "E92", {"start": v(5, 0) * mm, "end": v(5, 12) * mm, "construction": true});
            skLineSegment(sketch, "E93.bottom", {"start": v(5, 12) * mm, "end": v(39, 12) * mm});
            skLineSegment(sketch, "E93.top", {"start": v(5, -5) * mm, "end": v(39, -5) * mm});
            skLineSegment(sketch, "E93.left", {"start": v(5, 12) * mm, "end": v(5, -5) * mm});
            skLineSegment(sketch, "E93.right", {"start": v(39, 12) * mm, "end": v(39, -5) * mm});
            skLineSegment(sketch, "E94", {"start": v(5, -5) * mm, "end": v(0, -5) * mm});
            skLineSegment(sketch, "E95", {"start": v(0, -5) * mm, "end": v(0, -10.55) * mm});
            skLineSegment(sketch, "E96", {"start": v(0, -10.55) * mm, "end": v(44, -10.55) * mm});
            skLineSegment(sketch, "E97", {"start": v(44, -10.55) * mm, "end": v(44, -5) * mm});
            skLineSegment(sketch, "E98", {"start": v(44, -5) * mm, "end": v(39, -5) * mm});
            skLineSegment(sketch, "E99", {"start": v(10.55, 6.04) * mm, "end": v(10.47, -5) * mm});
            skArc(sketch, "E100.0", {"start": v(13.35, 5.92) * mm, "mid": v(12, 7.42) * mm, "end": v(10.55, 6.04) * mm});
            skArc(sketch, "E101.0", {"start": v(33.45, 5.9) * mm, "mid": v(32.1, 7.42) * mm, "end": v(30.65, 6) * mm});
            skLineSegment(sketch, "E102", {"start": v(13.35, 6.03) * mm, "end": v(12.92, -5) * mm});
            skLineSegment(sketch, "E103", {"start": v(30.65, 6) * mm, "end": v(30.22, -5) * mm});
            skLineSegment(sketch, "E104", {"start": v(33.44, 6.14) * mm, "end": v(33.45, -5) * mm});
            skSolve(sketch);
        }
        {
            var Q0;
            Q0=makeQuery(id+"F4.opExtrude","SWEPT_FACE",FACE,{"disambiguationData":[OSD([sQuery(id+"F3.wireOp",EDGE,"E22")])]});
            var sketch = newSketch(context, id + "F29", { "sketchPlane" : qUnion([Q0])});
            skLineSegment(sketch, "E105", {"start": v(12, 67.55) * mm, "end": v(12, 58.55) * mm, "construction": true});
            skLineSegment(sketch, "E106.bottom", {"start": v(7, 53.55) * mm, "end": v(17, 53.55) * mm});
            skLineSegment(sketch, "E106.top", {"start": v(7, 63.55) * mm, "end": v(17, 63.55) * mm});
            skLineSegment(sketch, "E106.left", {"start": v(7, 53.55) * mm, "end": v(7, 63.55) * mm});
            skLineSegment(sketch, "E106.right", {"start": v(17, 53.55) * mm, "end": v(17, 63.55) * mm});
            skPoint(sketch, "E106.middle", {"position": v(12, 58.55) * mm});
            skSolve(sketch);
        }
        {
            var Q0;
            Q0 = qSketchRegion(id + "F29", true);
            var Q1;
            Q1 = qConstructionFilter(qBodyType(qCreatedBy(id + "F29" ,EDGE), BodyType.WIRE), ConstructionObject.NO);
            extrude(context, id + "F30", {"entities" : qUnion([Q0]), "operationType" : NewBodyOperationType.REMOVE, "surfaceEntities" : qUnion([Q1]), "depth" : 25 * mm, "hasSecondDirection" : true, "secondDirectionOppositeDirection" : true, "secondDirectionDepth" : 25 * mm, "offsetDistance" : 25 * mm});
        }
        {
            var Q0;
            Q0=makeQuery(id+"F30.boolean.opBoolean","INTERSECT",EDGE,{"derivedFrom":[makeQuery(id+"F4.opExtrude","SWEPT_FACE",FACE,{"disambiguationData":[OSD([sQuery(id+"F3.wireOp",EDGE,"E22")])]}),makeQuery(id+"F30.opExtrude","SWEPT_FACE",FACE,{"disambiguationData":[OSD([sQuery(id+"F29.wireOp",EDGE,"E106.left")])]})]});
            var Q1;
            Q1=makeQuery(id+"F30.boolean.opBoolean","INTERSECT",EDGE,{"derivedFrom":[makeQuery(id+"F4.opExtrude","SWEPT_FACE",FACE,{"disambiguationData":[OSD([sQuery(id+"F3.wireOp",EDGE,"E24")])]}),makeQuery(id+"F30.opExtrude","SWEPT_FACE",FACE,{"disambiguationData":[OSD([sQuery(id+"F29.wireOp",EDGE,"E106.left")])]})]});
            var Q2;
            Q2=makeQuery(id+"F30.boolean.opBoolean","INTERSECT",EDGE,{"derivedFrom":[makeQuery(id+"F9.opFillet","BLEND_FACE",FACE,{"disambiguationData":[OSD([sQuery(id+"F3.wireOp",EDGE,"E15"),sQuery(id+"F3.wireOp",EDGE,"E21")])]}),makeQuery(id+"F30.opExtrude","SWEPT_FACE",FACE,{"disambiguationData":[OSD([sQuery(id+"F29.wireOp",EDGE,"E106.left")])]})]});
            var Q3;
            Q3=makeQuery(id+"F30.boolean.opBoolean","INTERSECT",EDGE,{"derivedFrom":[makeQuery(id+"F9.opFillet","BLEND_FACE",FACE,{"disambiguationData":[OSD([sQuery(id+"F3.wireOp",EDGE,"E15"),sQuery(id+"F3.wireOp",EDGE,"E21")])]}),makeQuery(id+"F30.opExtrude","SWEPT_FACE",FACE,{"disambiguationData":[OSD([sQuery(id+"F29.wireOp",EDGE,"E106.right")])]})]});
            var Q4;
            Q4=makeQuery(id+"F30.boolean.opBoolean","INTERSECT",EDGE,{"derivedFrom":[makeQuery(id+"F4.opExtrude","SWEPT_FACE",FACE,{"disambiguationData":[OSD([sQuery(id+"F3.wireOp",EDGE,"E22")])]}),makeQuery(id+"F30.opExtrude","SWEPT_FACE",FACE,{"disambiguationData":[OSD([sQuery(id+"F29.wireOp",EDGE,"E106.right")])]})]});
            var Q5;
            Q5=makeQuery(id+"F30.boolean.opBoolean","INTERSECT",EDGE,{"derivedFrom":[makeQuery(id+"F4.opExtrude","SWEPT_FACE",FACE,{"disambiguationData":[OSD([sQuery(id+"F3.wireOp",EDGE,"E24")])]}),makeQuery(id+"F30.opExtrude","SWEPT_FACE",FACE,{"disambiguationData":[OSD([sQuery(id+"F29.wireOp",EDGE,"E106.right")])]})]});
            fillet(context, id + "F31", {"entities" : qUnion([Q0, Q1, Q2, Q3, Q4, Q5]), "radius" : 3 * mm, "tangentPropagation" : true, "allowEdgeOverflow" : false});
        }
        {
            var Q0;
            Q0 = qSketchRegion(id + "F28", true);
            extrude(context, id + "F32", {"entities" : qUnion([Q0]), "depth" : 2 * mm});
        }
        {
            var Q0;
            Q0=makeQuery(id+"F32.opExtrude","CAP_FACE",FACE,{"disambiguationData":[OSD([sQuery(id+"F28.wireOp",EDGE,"E93.bottom"),sQuery(id+"F28.wireOp",EDGE,"E93.top"),sQuery(id+"F28.wireOp",EDGE,"E93.left"),sQuery(id+"F28.wireOp",EDGE,"E93.right"),sQuery(id+"F28.wireOp",EDGE,"E94"),sQuery(id+"F28.wireOp",EDGE,"E95"),sQuery(id+"F28.wireOp",EDGE,"E96"),sQuery(id+"F28.wireOp",EDGE,"E97"),sQuery(id+"F28.wireOp",EDGE,"E98"),sQuery(id+"F28.wireOp",EDGE,"E99"),sQuery(id+"F28.wireOp",EDGE,"E100.0"),sQuery(id+"F28.wireOp",EDGE,"E101.0"),sQuery(id+"F28.wireOp",EDGE,"E102"),sQuery(id+"F28.wireOp",EDGE,"E103"),sQuery(id+"F28.wireOp",EDGE,"E104")])],"isStart":false});
            var sketch = newSketch(context, id + "F33", { "sketchPlane" : qUnion([Q0])});
            skLineSegment(sketch, "E107.bottom", {"start": v(5, 12) * mm, "end": v(39, 12) * mm});
            skLineSegment(sketch, "E107.top", {"start": v(5, 0) * mm, "end": v(39, 0) * mm});
            skLineSegment(sketch, "E107.left", {"start": v(5, 12) * mm, "end": v(5, 0) * mm});
            skLineSegment(sketch, "E107.right", {"start": v(39, 12) * mm, "end": v(39, 0) * mm});
            skCircle(sketch, "E108.0", {"center": v(11.95, 6.03) * mm, "radius": 1.4 * mm});
            skCircle(sketch, "E109.0", {"center": v(32.05, 6.03) * mm, "radius": 1.4 * mm});
            skSolve(sketch);
        }
        {
            var Q0;
            Q0 = qSketchRegion(id + "F33", true);
            extrude(context, id + "F34", {"entities" : qUnion([Q0]), "depth" : 6 * mm});
        }
        {
            var Q0;
            Q0=makeQuery(id+"F4.opExtrude","CAP_FACE",FACE,{"disambiguationData":[OSD([sQuery(id+"F3.wireOp",EDGE,"E14"),sQuery(id+"F3.wireOp",EDGE,"E15"),sQuery(id+"F3.wireOp",EDGE,"E16"),sQuery(id+"F3.wireOp",EDGE,"E19.0"),sQuery(id+"F3.wireOp",EDGE,"E20.0"),sQuery(id+"F3.wireOp",EDGE,"E21"),sQuery(id+"F3.wireOp",EDGE,"E22"),sQuery(id+"F3.wireOp",EDGE,"E23"),sQuery(id+"F3.wireOp",EDGE,"E24")])],"isStart":false});
            var sketch = newSketch(context, id + "F35", { "sketchPlane" : qUnion([Q0])});
            skLineSegment(sketch, "E110.bottom", {"start": v(0, 0) * mm, "end": v(40, 0) * mm});
            skLineSegment(sketch, "E110.top", {"start": v(0, -1) * mm, "end": v(40, -1) * mm});
            skLineSegment(sketch, "E110.left", {"start": v(0, 0) * mm, "end": v(0, -1) * mm});
            skLineSegment(sketch, "E110.right", {"start": v(40, 0) * mm, "end": v(40, -1) * mm});
            skSolve(sketch);
        }
        {
            var Q0;
            Q0 = qSketchRegion(id + "F35", true);
            extrude(context, id + "F36", {"entities" : qUnion([Q0]), "operationType" : NewBodyOperationType.REMOVE, "oppositeDirection" : true, "depth" : 25 * mm});
        }
        {
            var Q0;
            Q0=makeQuery(id+"F4.opExtrude","SWEPT_EDGE",EDGE,{"disambiguationData":[OSD([sQuery(id+"F3.wireOp",EDGE,"E23"),sQuery(id+"F3.wireOp",EDGE,"E24")])]});
            var Q1;
            Q1=makeQuery(id+"F4.opExtrude","SWEPT_EDGE",EDGE,{"disambiguationData":[OSD([sQuery(id+"F3.wireOp",EDGE,"E22"),sQuery(id+"F3.wireOp",EDGE,"E23")])]});
            fillet(context, id + "F37", {"entities" : qUnion([Q0, Q1]), "radius" : 1 * mm, "tangentPropagation" : true, "allowEdgeOverflow" : false});
        }
        {
            var Q0;
            Q0=makeQuery(id+"F13.opExtrude","SWEPT_EDGE",EDGE,{"disambiguationData":[OSD([sQuery(id+"F3.wireOp",EDGE,"E15"),sQuery(id+"F10.wireOp",EDGE,"E46.top"),sQuery(id+"F10.wireOp",EDGE,"E46.right")])]});
            var Q1;
            Q1=makeQuery(id+"F13.opExtrude","SWEPT_EDGE",EDGE,{"disambiguationData":[OSD([sQuery(id+"F10.wireOp",EDGE,"E46.bottom"),sQuery(id+"F10.wireOp",EDGE,"E46.right")])]});
            var Q2;
            Q2=makeQuery(id+"F13.opExtrude","SWEPT_EDGE",EDGE,{"disambiguationData":[OSD([sQuery(id+"F10.wireOp",EDGE,"E46.top"),sQuery(id+"F10.wireOp",EDGE,"E46.left")])]});
            var Q3;
            Q3=makeQuery(id+"F13.opExtrude","SWEPT_EDGE",EDGE,{"disambiguationData":[OSD([sQuery(id+"F10.wireOp",EDGE,"E46.bottom"),sQuery(id+"F10.wireOp",EDGE,"E46.left")])]});
            fillet(context, id + "F38", {"entities" : qUnion([Q0, Q1, Q2, Q3]), "radius" : 1 * mm, "tangentPropagation" : true, "allowEdgeOverflow" : false});
        }
        {
            var Q0;
            Q0=makeQuery(id+"F11.opExtrude","SWEPT_EDGE",EDGE,{"disambiguationData":[OSD([sQuery(id+"F10.wireOp",EDGE,"E46.bottom"),sQuery(id+"F10.wireOp",EDGE,"E47.0")])]});
            var Q1;
            Q1=makeQuery(id+"F11.opExtrude","SWEPT_EDGE",EDGE,{"disambiguationData":[OSD([sQuery(id+"F10.wireOp",EDGE,"E46.top"),sQuery(id+"F10.wireOp",EDGE,"E51.0")])]});
            var Q2;
            Q2=makeQuery(id+"F11.opExtrude","SWEPT_EDGE",EDGE,{"disambiguationData":[OSD([sQuery(id+"F10.wireOp",EDGE,"E47.0"),sQuery(id+"F10.wireOp",EDGE,"E48.0")])]});
            var Q3;
            Q3=makeQuery(id+"F11.opExtrude","SWEPT_EDGE",EDGE,{"disambiguationData":[OSD([sQuery(id+"F10.wireOp",EDGE,"E50.0"),sQuery(id+"F10.wireOp",EDGE,"E51.0")])]});
            var Q4;
            {var subQ0=sQuery(id+"F10.wireOp",EDGE,"E49.0");Q4=makeQuery(id+"F15.boolean.opBoolean","SPLIT",EDGE,{"disambiguationData":[topologyDisambiguationEdgeConnected([makeQuery(id+"F15.opRevolve","SWEPT_FACE",FACE,{"disambiguationData":[OSD([sQuery(id+"F14.wireOp",EDGE,"E60.0")])]})])],"derivedFrom":makeQuery(id+"F11.opExtrude","SWEPT_EDGE",EDGE,{"disambiguationData":[OSD([subQ0,sQuery(id+"F10.wireOp",EDGE,"E50.0")])]})});}
            var Q5;
            {var subQ0=sQuery(id+"F10.wireOp",EDGE,"E49.0");Q5=makeQuery(id+"F15.boolean.opBoolean","SPLIT",EDGE,{"disambiguationData":[topologyDisambiguationEdgeConnected([makeQuery(id+"F15.opRevolve","SWEPT_FACE",FACE,{"disambiguationData":[OSD([sQuery(id+"F14.wireOp",EDGE,"E60.2")])]})])],"derivedFrom":makeQuery(id+"F11.opExtrude","SWEPT_EDGE",EDGE,{"disambiguationData":[OSD([sQuery(id+"F10.wireOp",EDGE,"E48.0"),subQ0])]})});}
            var Q6;
            Q6=makeQuery(id+"F11.opExtrude","SWEPT_EDGE",EDGE,{"disambiguationData":[OSD([sQuery(id+"F10.wireOp",EDGE,"E46.bottom"),sQuery(id+"F10.wireOp",EDGE,"E56.0")])]});
            var Q7;
            Q7=makeQuery(id+"F11.opExtrude","SWEPT_EDGE",EDGE,{"disambiguationData":[OSD([sQuery(id+"F10.wireOp",EDGE,"E55.0"),sQuery(id+"F10.wireOp",EDGE,"E56.0")])]});
            var Q8;
            Q8=makeQuery(id+"F11.opExtrude","SWEPT_EDGE",EDGE,{"disambiguationData":[OSD([sQuery(id+"F10.wireOp",EDGE,"E52.0"),sQuery(id+"F10.wireOp",EDGE,"E53.0")])]});
            var Q9;
            Q9=makeQuery(id+"F11.opExtrude","SWEPT_EDGE",EDGE,{"disambiguationData":[OSD([sQuery(id+"F10.wireOp",EDGE,"E46.top"),sQuery(id+"F10.wireOp",EDGE,"E52.0")])]});
            var Q10;
            {var subQ0=sQuery(id+"F10.wireOp",EDGE,"E54.0");Q10=makeQuery(id+"F15.boolean.opBoolean","SPLIT",EDGE,{"disambiguationData":[topologyDisambiguationEdgeConnected([makeQuery(id+"F15.opRevolve","SWEPT_FACE",FACE,{"disambiguationData":[OSD([sQuery(id+"F14.wireOp",EDGE,"E60.2")])]})])],"derivedFrom":makeQuery(id+"F11.opExtrude","SWEPT_EDGE",EDGE,{"disambiguationData":[OSD([subQ0,sQuery(id+"F10.wireOp",EDGE,"E55.0")])]})});}
            var Q11;
            {var subQ0=sQuery(id+"F10.wireOp",EDGE,"E54.0");Q11=makeQuery(id+"F15.boolean.opBoolean","SPLIT",EDGE,{"disambiguationData":[topologyDisambiguationEdgeConnected([makeQuery(id+"F15.opRevolve","SWEPT_FACE",FACE,{"disambiguationData":[OSD([sQuery(id+"F14.wireOp",EDGE,"E60.0")])]})])],"derivedFrom":makeQuery(id+"F11.opExtrude","SWEPT_EDGE",EDGE,{"disambiguationData":[OSD([sQuery(id+"F10.wireOp",EDGE,"E53.0"),subQ0])]})});}
            var Q12;
            Q12=makeQuery(id+"F15.boolean.opBoolean","INTERSECT",EDGE,{"disambiguationData":[OD(1.0)],"derivedFrom":[makeQuery(id+"F11.opExtrude","CAP_FACE",FACE,{"disambiguationData":[OSD([sQuery(id+"F10.wireOp",EDGE,"E46.bottom"),sQuery(id+"F10.wireOp",EDGE,"E46.top"),sQuery(id+"F10.wireOp",EDGE,"E47.0"),sQuery(id+"F10.wireOp",EDGE,"E48.0"),sQuery(id+"F10.wireOp",EDGE,"E49.0"),sQuery(id+"F10.wireOp",EDGE,"E50.0"),sQuery(id+"F10.wireOp",EDGE,"E51.0"),sQuery(id+"F10.wireOp",EDGE,"E52.0"),sQuery(id+"F10.wireOp",EDGE,"E53.0"),sQuery(id+"F10.wireOp",EDGE,"E54.0"),sQuery(id+"F10.wireOp",EDGE,"E55.0"),sQuery(id+"F10.wireOp",EDGE,"E56.0")])],"isStart":false}),makeQuery(id+"F15.opRevolve","SWEPT_FACE",FACE,{"disambiguationData":[OSD([sQuery(id+"F14.wireOp",EDGE,"E60.1")])]})]});
            var Q13;
            Q13=makeQuery(id+"F15.boolean.opBoolean","INTERSECT",EDGE,{"disambiguationData":[OD(0.0)],"derivedFrom":[makeQuery(id+"F11.opExtrude","CAP_FACE",FACE,{"disambiguationData":[OSD([sQuery(id+"F10.wireOp",EDGE,"E46.bottom"),sQuery(id+"F10.wireOp",EDGE,"E46.top"),sQuery(id+"F10.wireOp",EDGE,"E47.0"),sQuery(id+"F10.wireOp",EDGE,"E48.0"),sQuery(id+"F10.wireOp",EDGE,"E49.0"),sQuery(id+"F10.wireOp",EDGE,"E50.0"),sQuery(id+"F10.wireOp",EDGE,"E51.0"),sQuery(id+"F10.wireOp",EDGE,"E52.0"),sQuery(id+"F10.wireOp",EDGE,"E53.0"),sQuery(id+"F10.wireOp",EDGE,"E54.0"),sQuery(id+"F10.wireOp",EDGE,"E55.0"),sQuery(id+"F10.wireOp",EDGE,"E56.0")])],"isStart":false}),makeQuery(id+"F15.opRevolve","SWEPT_FACE",FACE,{"disambiguationData":[OSD([sQuery(id+"F14.wireOp",EDGE,"E60.1")])]})]});
            var Q14;
            Q14=makeQuery(id+"F11.opExtrude","CAP_EDGE",EDGE,{"disambiguationData":[OSD([sQuery(id+"F10.wireOp",EDGE,"E49.0")])],"isStart":false});
            var Q15;
            Q15=makeQuery(id+"F11.opExtrude","CAP_EDGE",EDGE,{"disambiguationData":[OSD([sQuery(id+"F10.wireOp",EDGE,"E54.0")])],"isStart":false});
            var Q16;
            Q16=makeQuery(id+"F11.opExtrude","CAP_EDGE",EDGE,{"disambiguationData":[OSD([sQuery(id+"F10.wireOp",EDGE,"E47.0")])],"isStart":false});
            var Q17;
            Q17=makeQuery(id+"F11.opExtrude","CAP_EDGE",EDGE,{"disambiguationData":[OSD([sQuery(id+"F10.wireOp",EDGE,"E51.0")])],"isStart":false});
            var Q18;
            Q18=makeQuery(id+"F11.opExtrude","CAP_EDGE",EDGE,{"disambiguationData":[OSD([sQuery(id+"F10.wireOp",EDGE,"E56.0")])],"isStart":false});
            var Q19;
            Q19=makeQuery(id+"F11.opExtrude","CAP_EDGE",EDGE,{"disambiguationData":[OSD([sQuery(id+"F10.wireOp",EDGE,"E52.0")])],"isStart":false});
            fillet(context, id + "F39", {"entities" : qUnion([Q0, Q1, Q2, Q3, Q4, Q5, Q6, Q7, Q8, Q9, Q10, Q11, Q12, Q13, Q14, Q15, Q16, Q17, Q18, Q19]), "radius" : 0.5 * mm, "tangentPropagation" : true, "allowEdgeOverflow" : false});
        }
    });
